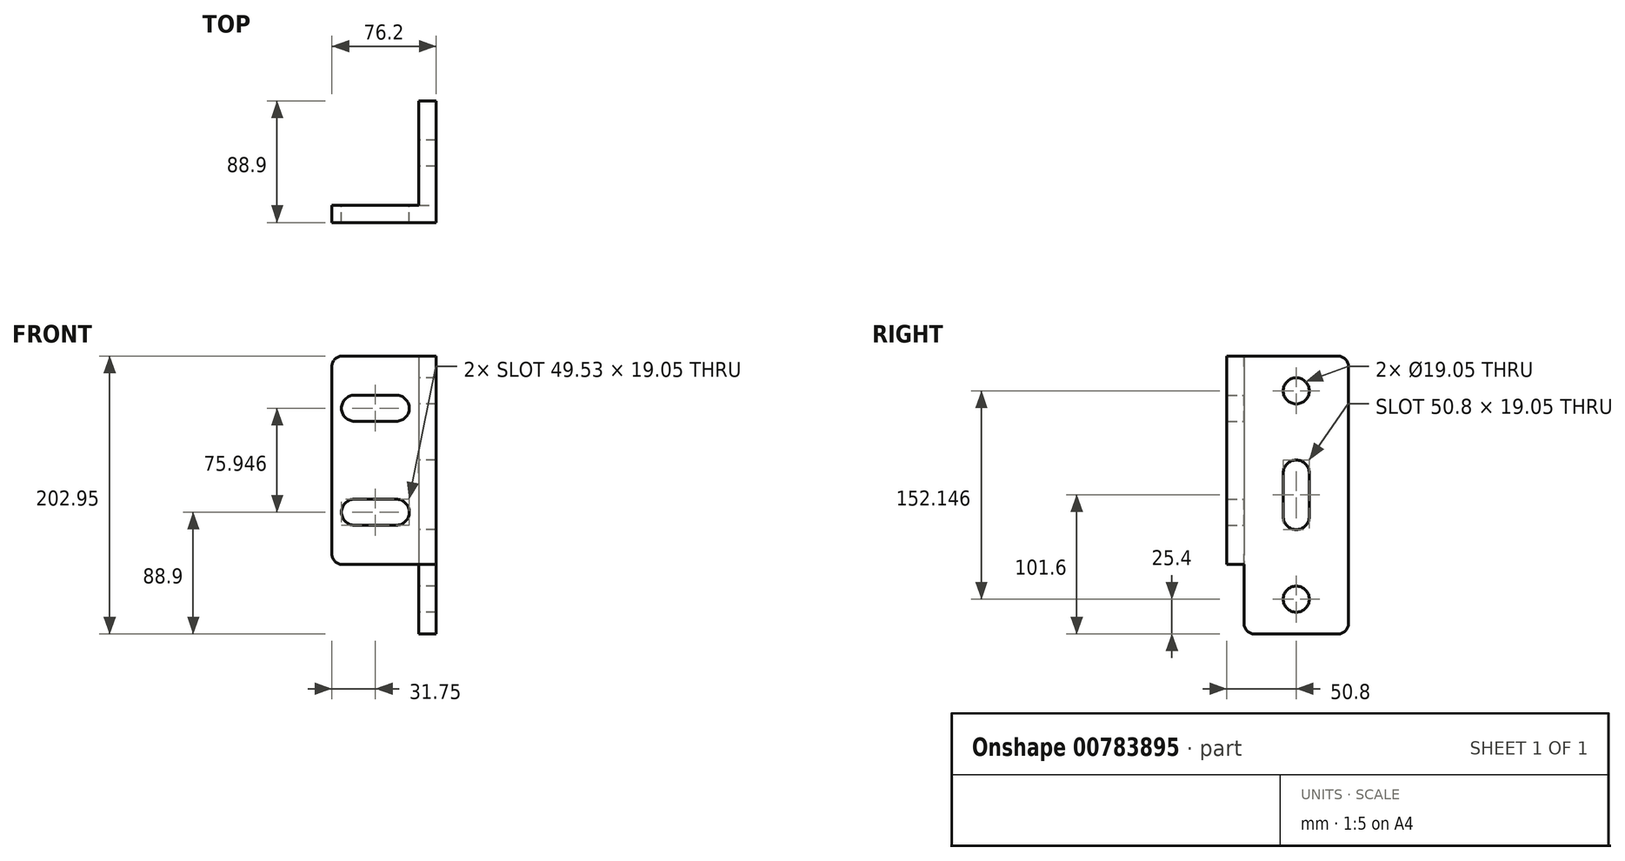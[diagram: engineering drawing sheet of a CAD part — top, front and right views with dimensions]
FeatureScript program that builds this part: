
annotation { "Feature Type Name" : "Feature", "Feature Type Description" : "" }
export const myFeature = defineFeature(function(context is Context, id is Id, definition is map)
    precondition{}
    {
        {
            var Q0;
            Q0=qCreatedBy(makeId("Top.planeOp"),FACE);
            var sketch = newSketch(context, id + "F0", { "sketchPlane" : qUnion([Q0])});
            skLineSegment(sketch, "E0", {"start": v(0, 0) * mm, "end": v(0, 12.7) * mm});
            skLineSegment(sketch, "E1", {"start": v(0, 0) * mm, "end": v(76.2, 0) * mm});
            skLineSegment(sketch, "E2", {"start": v(76.2, 0) * mm, "end": v(76.2, 88.9) * mm});
            skLineSegment(sketch, "E3", {"start": v(76.2, 88.9) * mm, "end": v(63.5, 88.9) * mm});
            skLineSegment(sketch, "E4", {"start": v(0, 12.7) * mm, "end": v(63.5, 12.7) * mm});
            skLineSegment(sketch, "E5", {"start": v(63.5, 12.7) * mm, "end": v(63.5, 88.9) * mm});
            skSolve(sketch);
        }
        {
            var Q0;
            Q0=makeQuery(id+"F0.imprint","IMPRINT",FACE,{"disambiguationData":[TD([[makeQuery(id+"F0.imprint","IMPRINT",EDGE,{"derivedFrom":sQuery(id+"F0.wireOp",EDGE,"E0")}),-1.0]])]});
            extrude(context, id + "F1", {"entities" : qUnion([Q0]), "depth" : 152.15 * mm, "offsetDistance" : 25.4 * mm});
        }
        {
            var Q0;
            Q0=makeQuery(id+"F1.opExtrude","CAP_FACE",FACE,{"disambiguationData":[OSD([sQuery(id+"F0.wireOp",EDGE,"E0"),sQuery(id+"F0.wireOp",EDGE,"E1"),sQuery(id+"F0.wireOp",EDGE,"E2"),sQuery(id+"F0.wireOp",EDGE,"E3"),sQuery(id+"F0.wireOp",EDGE,"E4"),sQuery(id+"F0.wireOp",EDGE,"E5")])],"isStart":true});
            var sketch = newSketch(context, id + "F2", { "sketchPlane" : qUnion([Q0])});
            skLineSegment(sketch, "E6.0", {"start": v(76.2, -88.9) * mm, "end": v(63.5, -88.9) * mm});
            skLineSegment(sketch, "E6.1", {"start": v(63.5, -12.7) * mm, "end": v(63.5, -88.9) * mm});
            skLineSegment(sketch, "E7", {"start": v(63.5, -12.7) * mm, "end": v(76.2, -12.7) * mm});
            skLineSegment(sketch, "E8", {"start": v(76.2, -12.7) * mm, "end": v(76.2, -88.9) * mm});
            skSolve(sketch);
        }
        {
            var Q0;
            Q0=makeQuery(id+"F2.imprint","IMPRINT",FACE,{"disambiguationData":[TD([[makeQuery(id+"F2.imprint","IMPRINT",EDGE,{"derivedFrom":sQuery(id+"F2.wireOp",EDGE,"E6.0")}),-1.0]])]});
            extrude(context, id + "F3", {"entities" : qUnion([Q0]), "operationType" : NewBodyOperationType.ADD, "depth" : 50.8 * mm, "offsetDistance" : 25.4 * mm});
        }
        {
            var Q0;
            Q0=makeQuery(id+"F1.opExtrude","CAP_EDGE",EDGE,{"disambiguationData":[OSD([sQuery(id+"F0.wireOp",EDGE,"E0")])],"isStart":true});
            var Q1;
            Q1=makeQuery(id+"F1.opExtrude","CAP_EDGE",EDGE,{"disambiguationData":[OSD([sQuery(id+"F0.wireOp",EDGE,"E0")])],"isStart":false});
            fillet(context, id + "F4", {"entities" : qUnion([Q0, Q1]), "radius" : 7.62 * mm, "tangentPropagation" : true, "allowEdgeOverflow" : false});
        }
        {
            var Q0;
            Q0=makeQuery(id+"F1.opExtrude","CAP_EDGE",EDGE,{"disambiguationData":[OSD([sQuery(id+"F0.wireOp",EDGE,"E3")])],"isStart":false});
            fillet(context, id + "F5", {"entities" : qUnion([Q0]), "radius" : 7.62 * mm, "tangentPropagation" : true, "allowEdgeOverflow" : false});
        }
        {
            var Q0;
            Q0=makeQuery(id+"F3.opExtrude","CAP_EDGE",EDGE,{"disambiguationData":[OSD([sQuery(id+"F2.wireOp",EDGE,"E7")])],"isStart":false});
            var Q1;
            Q1=makeQuery(id+"F3.opExtrude","CAP_EDGE",EDGE,{"disambiguationData":[OSD([sQuery(id+"F2.wireOp",EDGE,"E6.0")])],"isStart":false});
            fillet(context, id + "F6", {"entities" : qUnion([Q0, Q1]), "radius" : 7.62 * mm, "tangentPropagation" : true, "allowEdgeOverflow" : false});
        }
        {
            var Q0;
            Q0=makeQuery(id+"F1.opExtrude","SWEPT_FACE",FACE,{"disambiguationData":[OSD([sQuery(id+"F0.wireOp",EDGE,"E4")])]});
            var sketch = newSketch(context, id + "F7", { "sketchPlane" : qUnion([Q0])});
            skLineSegment(sketch, "E9", {"start": v(-31.75, 152.15) * mm, "end": v(-31.75, 0) * mm, "construction": true});
            skLineSegment(sketch, "E10", {"start": v(-60.96, 76.07) * mm, "end": v(0, 76.07) * mm, "construction": true});
            skLineSegment(sketch, "E11", {"start": v(-60.96, 114.05) * mm, "end": v(0, 114.05) * mm, "construction": true});
            skLineSegment(sketch, "E12", {"start": v(-58.42, 38.1) * mm, "end": v(0, 38.1) * mm, "construction": true});
            skLineSegment(sketch, "E13.bottom", {"start": v(-16.5, 104.52) * mm, "end": v(-46.99, 104.52) * mm});
            skLineSegment(sketch, "E13.top", {"start": v(-16.51, 123.57) * mm, "end": v(-47, 123.57) * mm});
            skPoint(sketch, "E13.middle", {"position": v(-31.75, 114.05) * mm});
            skLineSegment(sketch, "E14.bottom", {"start": v(-16.5, 28.58) * mm, "end": v(-46.99, 28.58) * mm});
            skLineSegment(sketch, "E14.top", {"start": v(-16.5, 47.62) * mm, "end": v(-46.99, 47.62) * mm});
            skPoint(sketch, "E14.middle", {"position": v(-31.75, 38.1) * mm});
            skArc(sketch, "E15", {"start": v(-16.51, 123.57) * mm, "mid": v(-6.99, 114.05) * mm, "end": v(-16.5, 104.52) * mm});
            skArc(sketch, "E16", {"start": v(-46.99, 104.52) * mm, "mid": v(-56.52, 114.05) * mm, "end": v(-47, 123.57) * mm});
            skArc(sketch, "E17", {"start": v(-46.99, 28.57) * mm, "mid": v(-56.52, 38.1) * mm, "end": v(-46.99, 47.62) * mm});
            skArc(sketch, "E18", {"start": v(-16.5, 28.58) * mm, "mid": v(-6.98, 38.1) * mm, "end": v(-16.5, 47.63) * mm});
            skSolve(sketch);
        }
        {
            var Q0;
            Q0=makeQuery(id+"F7.imprint","IMPRINT",FACE,{"disambiguationData":[TD([[makeQuery(id+"F7.imprint","IMPRINT",EDGE,{"derivedFrom":sQuery(id+"F7.wireOp",EDGE,"E14.bottom")}),-1.0]])]});
            var Q1;
            Q1=makeQuery(id+"F7.imprint","IMPRINT",FACE,{"disambiguationData":[TD([[makeQuery(id+"F7.imprint","IMPRINT",EDGE,{"derivedFrom":sQuery(id+"F7.wireOp",EDGE,"E13.bottom")}),-1.0]])]});
            extrude(context, id + "F8", {"entities" : qUnion([Q0, Q1]), "operationType" : NewBodyOperationType.REMOVE, "oppositeDirection" : true, "depth" : 25.4 * mm, "offsetDistance" : 25.4 * mm});
        }
        {
            var Q0;
            Q0=makeQuery(id+"F3.boolean.opBoolean","MERGE",FACE,{"derivedFrom":[makeQuery(id+"F1.opExtrude","SWEPT_FACE",FACE,{"disambiguationData":[OSD([sQuery(id+"F0.wireOp",EDGE,"E5")])]}),makeQuery(id+"F3.opExtrude","SWEPT_FACE",FACE,{"disambiguationData":[OSD([sQuery(id+"F2.wireOp",EDGE,"E6.1")])]})]});
            var sketch = newSketch(context, id + "F9", { "sketchPlane" : qUnion([Q0])});
            skLineSegment(sketch, "E19", {"start": v(-88.9, -25.4) * mm, "end": v(-12.7, -25.4) * mm, "construction": true});
            skLineSegment(sketch, "E20", {"start": v(-88.9, 50.8) * mm, "end": v(-15.24, 50.8) * mm, "construction": true});
            skLineSegment(sketch, "E21", {"start": v(-88.9, 126.75) * mm, "end": v(-15.24, 126.75) * mm, "construction": true});
            skLineSegment(sketch, "E22", {"start": v(-50.8, -50.8) * mm, "end": v(-50.8, 152.15) * mm, "construction": true});
            skCircle(sketch, "E23", {"center": v(-50.8, -25.4) * mm, "radius": 9.53 * mm});
            skCircle(sketch, "E24", {"center": v(-50.8, 126.75) * mm, "radius": 9.53 * mm});
            skLineSegment(sketch, "E25.left", {"start": v(-41.28, 66.68) * mm, "end": v(-41.28, 34.93) * mm});
            skLineSegment(sketch, "E25.right", {"start": v(-60.33, 66.67) * mm, "end": v(-60.33, 34.92) * mm});
            skPoint(sketch, "E25.middle", {"position": v(-50.8, 50.8) * mm});
            skArc(sketch, "E26", {"start": v(-41.28, 34.93) * mm, "mid": v(-50.8, 25.4) * mm, "end": v(-60.32, 34.92) * mm});
            skArc(sketch, "E27", {"start": v(-41.28, 66.68) * mm, "mid": v(-50.8, 76.2) * mm, "end": v(-60.32, 66.67) * mm});
            skSolve(sketch);
        }
        {
            var Q0;
            Q0=makeQuery(id+"F9.imprint","IMPRINT",FACE,{"disambiguationData":[TD([[makeQuery(id+"F9.imprint","IMPRINT",EDGE,{"derivedFrom":sQuery(id+"F9.wireOp",EDGE,"E23")}),1.0]])]});
            var Q1;
            Q1=makeQuery(id+"F9.imprint","IMPRINT",FACE,{"disambiguationData":[TD([[makeQuery(id+"F9.imprint","IMPRINT",EDGE,{"derivedFrom":sQuery(id+"F9.wireOp",EDGE,"E25.left")}),-1.0]])]});
            var Q2;
            Q2=makeQuery(id+"F9.imprint","IMPRINT",FACE,{"disambiguationData":[TD([[makeQuery(id+"F9.imprint","IMPRINT",EDGE,{"derivedFrom":sQuery(id+"F9.wireOp",EDGE,"E24")}),1.0]])]});
            extrude(context, id + "F10", {"entities" : qUnion([Q0, Q1, Q2]), "operationType" : NewBodyOperationType.REMOVE, "endBound" : BoundingType.THROUGH_ALL, "oppositeDirection" : true, "depth" : 25.4 * mm, "offsetDistance" : 25.4 * mm});
        }
    });
